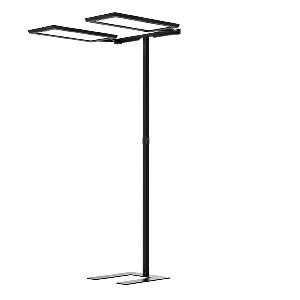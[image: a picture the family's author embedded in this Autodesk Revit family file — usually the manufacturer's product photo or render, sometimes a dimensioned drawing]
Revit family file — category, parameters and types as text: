
# Revit family: yara_doubleu_-_yus_2_15000_840_rx_sw_cee_s0_c_114268000-00813289_0bd9
name_source: partatom
category: Lighting Fixtures
units: mm (PartAtom-declared; Revit-internal decimal feet)

## family parameters
Cut with Voids When Loaded = No
Host = Face
Light Source = No
Part Type = Normal
Room Calculation Point = No
Round Connector Dimension = Use Diameter
Shared = No

## types (1)
- YARA.doubleU - YUS 2/15000/840/RX/SW/CEE/S0/C (1 x LED, 15000 lm, 4000K)
    Apparent Load = 214 VA
    Approval mark = CE
    CIE Flux Codes = 58 87 97 13 100
    Color Rendering = 80-89
    Color Temperature = 4000K
    Control Gear = Electronic ballast
    Default Elevation = 1800 mm
    Description = YUS 2/15000/840/RX/SW/CEE/S0/C|Free-standing luminaire|light source: LED Cold white   |work equipment: Electronic ballast DALI|connected load: 220-240 V, 50/60 Hz|Power consumption: approx. 210 W|power factor: approx. 0,966|luminous flux: 30000 lm|luminous efficacy: 142 lm/W|light distribution: Direct/indirect|direct ratio: approx. 13 %|color rendering index (CRI): >= 80|chromaticity tolerance:  3 SDCM|technology: Multiple daylight-dependent motion sensors|operation: Wireless switch|luminaire body|material: Aluminium/plastic|surface: Powder coatet|colour: Black|lamp cover: Acrylic (PMMA)|tubular section|material: Steel tube|surface: Powder-coated|Form: Tubular section upright|colour of tubular section: Black|luminaire base|Form: C-form flat|weight (net): approx. 26.0 kg|mains lead: 3.00 m Mains plug CEE 7/VII|Fastening: Floor standing base|glare control: Conical prismatic screen|luminance(L65): <= 2700 cd/m|unified glare rating(4H 8H): <=  16|special features: App control, Asymmetric radiation, Direct and indirect lighting component with edge light and light guidetechnology for a homogeneous light exit, Flicker-free, LTX multisensor for workplace optimisation, Magnetic control panel, freely positionable, Optional LTX Cloud connection, TALK Bluetooth|Approval mark: VDE - ENEC|
    Frequency = 50 Hz, 60 Hz
    Height = 24 mm  [stored 0.0787402 ft]
    Lamp = 1 x LED
    Lamp Light Flux = 15000 lm
    Lamp count = 1
    Length = 690 mm
    Luminous efficacy = 140 lm/W
    Manufacturer = Waldmann
    ModVariant = No
    Model = 114268000-00813289
    Mounting Place = Floor
    Mounting Type = Freestanding
    Number of Poles = 1
    OnlyDefault = Yes
    Power Factor = 1
    Product Name = YARA.doubleU - YUS 2/15000/840/RX/SW/CEE/S0/C
    Product group = Free standing luminaire
    ProductGroupID = 13
    Protection Class = Protection class I
    Protection Degree = IP 20
    RLX_Detail_Level = 1
    RlxData = <blob elided: 71377 chars, md5=fe21fe7b>
    Socket = socket
    Standby Power = 0 W
    System Light Flux = 30000 lm
    System Power = 214 W
    Type Comments = Product without accessories
    Type Image = yus-rx-sw-c.jpg
    URL = http://relux.com
    VarID = ---
    Voltage = 230 V
    Voltage Range = 220-240 V
    Weight = 0.00 kg
    Width = 358 mm

note: [stored X ft] marks values corroborated as IEEE doubles in the binary element streams (Revit-internal decimal feet)

## geometry (parser evidence)
native form markers: Blend x4, Sweep x20
no freeform markers — native parametric forms only
